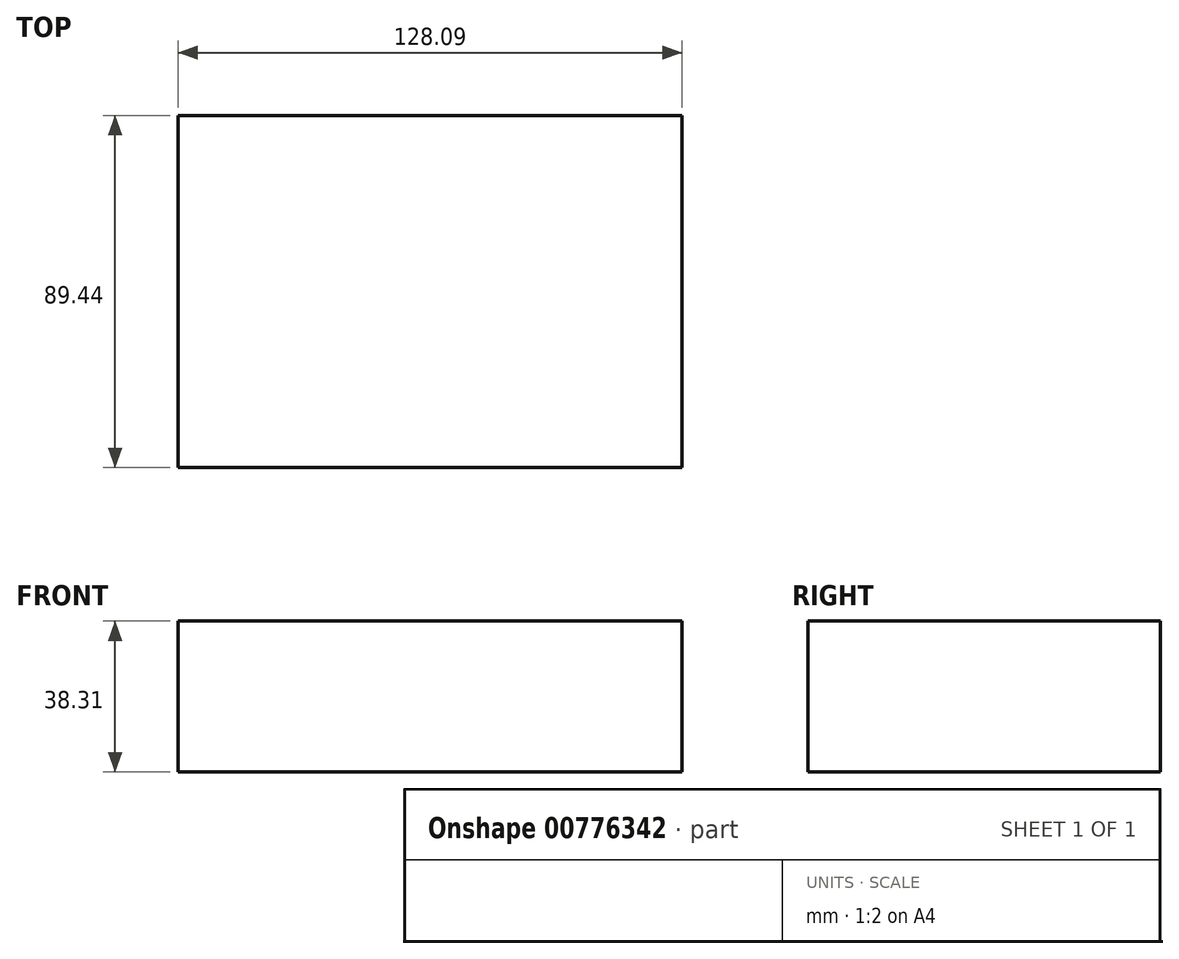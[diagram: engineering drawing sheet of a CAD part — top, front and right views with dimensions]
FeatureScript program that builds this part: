
annotation { "Feature Type Name" : "Feature", "Feature Type Description" : "" }
export const myFeature = defineFeature(function(context is Context, id is Id, definition is map)
    precondition{}
    {
        {
            var Q0;
            Q0=qCreatedBy(makeId("Front.planeOp"),FACE);
            var sketch = newSketch(context, id + "F0", { "sketchPlane" : qUnion([Q0])});
            skCircle(sketch, "E0", {"center": v(-18, 18.72) * mm, "radius": 28.88 * mm});
            skLineSegment(sketch, "E1.bottom", {"start": v(-56.82, 21.96) * mm, "end": v(71.27, 21.96) * mm});
            skLineSegment(sketch, "E1.top", {"start": v(-56.82, -16.35) * mm, "end": v(71.27, -16.35) * mm});
            skLineSegment(sketch, "E1.left", {"start": v(-56.82, 21.96) * mm, "end": v(-56.82, -16.35) * mm});
            skLineSegment(sketch, "E1.right", {"start": v(71.27, 21.96) * mm, "end": v(71.27, -16.35) * mm});
            skSolve(sketch);
        }
        {
            var Q0;
            Q0=makeQuery(id+"F0.imprint","IMPRINT",FACE,{"disambiguationData":[TD([[makeQuery(id+"F0.imprint","IMPRINT",EDGE,{"derivedFrom":sQuery(id+"F0.wireOp",EDGE,"E1.top")}),1.0]])]});
            var Q1;
            {var subQ0=sQuery(id+"F0.wireOp",EDGE,"E1.bottom");var subQ1=sQuery(id+"F0.wireOp",EDGE,"E0");var subQ2=makeQuery(id+"F0.imprint","INTERSECT",VERTEX,{"disambiguationData":[OD(0.0)],"derivedFrom":[subQ1,subQ0]});Q1=makeQuery(id+"F0.imprint","IMPRINT",FACE,{"disambiguationData":[TD([[makeQuery(id+"F0.imprint","IMPRINT",EDGE,{"disambiguationData":[TD([[subQ2,1.0]])],"derivedFrom":subQ1}),1.0]])]});}
            extrude(context, id + "F1", {"entities" : qUnion([Q0, Q1]), "depth" : 89.44 * mm, "offsetDistance" : 25.4 * mm});
        }
    });
